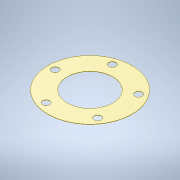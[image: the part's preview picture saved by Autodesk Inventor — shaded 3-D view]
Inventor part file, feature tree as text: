
AUTODESK INVENTOR PART (.ipt)
format: ipt  version: 2020 (Build 240168000, 168)  size: 122,368 bytes
history: native  units: mm
features: extrude x2, sketch x2
ambient origin geometry x8: Origin, YZ Plane, XZ Plane, XY Plane, X Axis, Y Axis, Z Axis, Center Point
bodies: Solid1 (feature_tree)
feature tree (4):
  extrude  "Extrusion1"  Depth=19.0mm
  extrude  "Extrusion2"  Depth=14.5mm
  sketch  "Sketch1"  dims[d0=35.0mm d1=19.0mm]
  sketch  "Sketch2"  dims[d2=0.1mm d3=0.0mm d4=3.0mm d5=0.0mm d6=14.5mm d7=50.0mm d9=360.0deg d11=0.0mm d12=0.0mm]
